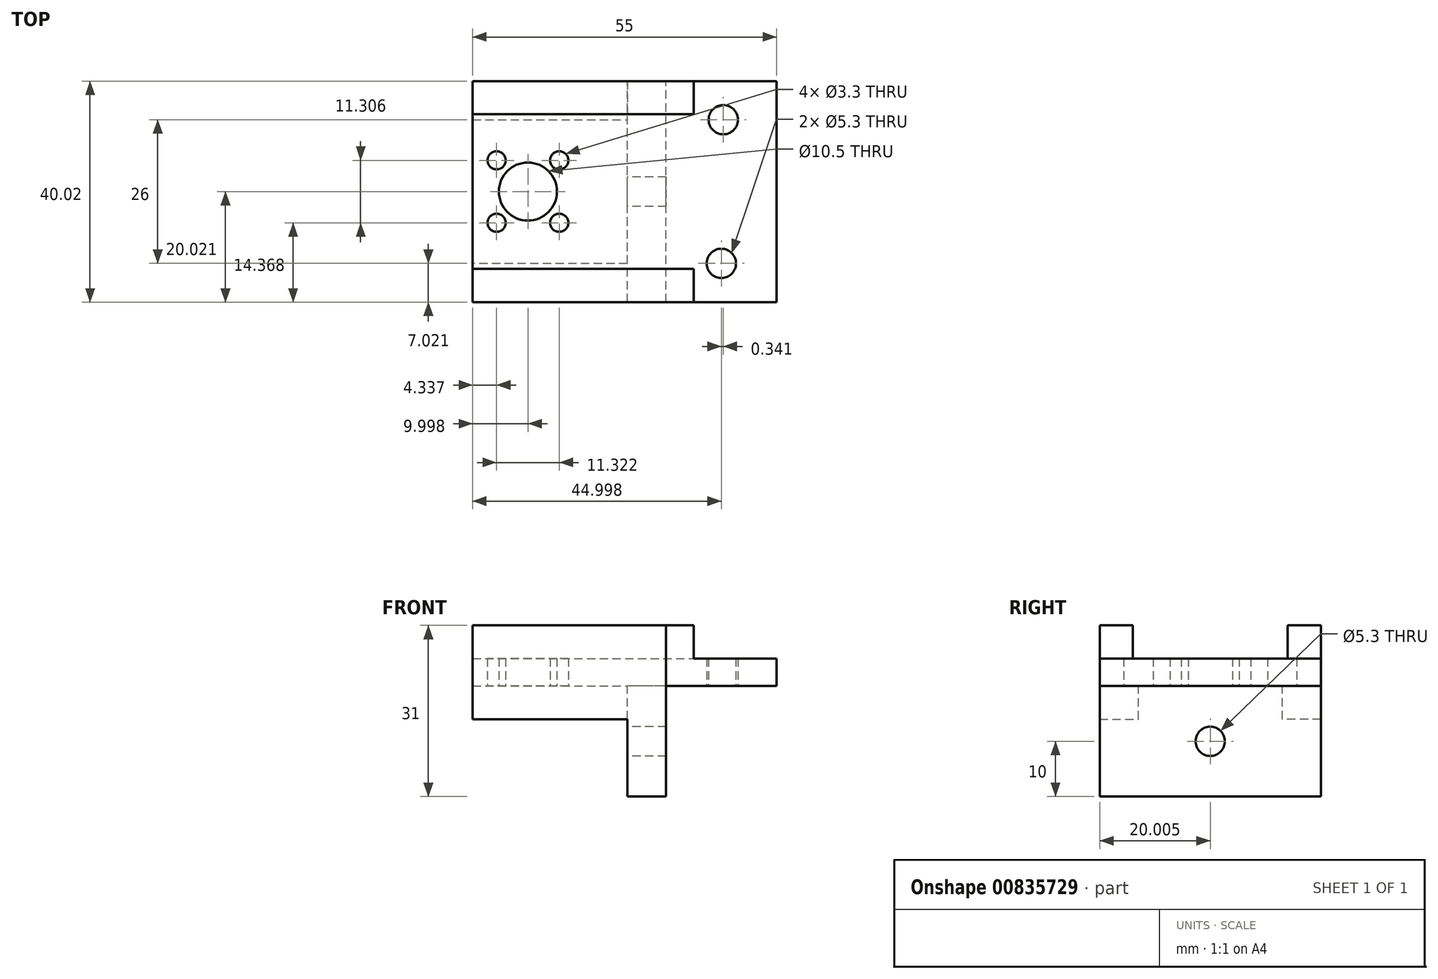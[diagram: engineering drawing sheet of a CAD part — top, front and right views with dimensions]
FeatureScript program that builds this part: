
annotation { "Feature Type Name" : "Feature", "Feature Type Description" : "" }
export const myFeature = defineFeature(function(context is Context, id is Id, definition is map)
    precondition{}
    {
        {
            var Q0;
            Q0=qCreatedBy(makeId("Top.planeOp"),FACE);
            var sketch = newSketch(context, id + "F0", { "sketchPlane" : qUnion([Q0])});
            skLineSegment(sketch, "E0.bottom", {"start": v(-49.07, -47.43) * mm, "end": v(-69.07, -47.43) * mm});
            skLineSegment(sketch, "E0.top", {"start": v(-49.07, -7.43) * mm, "end": v(-69.07, -7.43) * mm});
            skLineSegment(sketch, "E0.left", {"start": v(-49.07, -47.43) * mm, "end": v(-49.07, -7.43) * mm});
            skLineSegment(sketch, "E0.right", {"start": v(-69.07, -47.43) * mm, "end": v(-69.07, -7.43) * mm});
            skCircle(sketch, "E1", {"center": v(-59.07, -40.43) * mm, "radius": 2.65 * mm});
            skCircle(sketch, "E2", {"center": v(-58.73, -14.43) * mm, "radius": 2.65 * mm});
            skLineSegment(sketch, "E3.bottom", {"start": v(-69.07, -7.43) * mm, "end": v(-99.07, -7.43) * mm});
            skLineSegment(sketch, "E3.top", {"start": v(-69.07, -47.45) * mm, "end": v(-99.17, -47.45) * mm});
            skLineSegment(sketch, "E3.left", {"start": v(-69.07, -7.43) * mm, "end": v(-69.07, -47.45) * mm});
            skCircle(sketch, "E4", {"center": v(-94.07, -27.43) * mm, "radius": 5.25 * mm});
            skLineSegment(sketch, "E5.bottom", {"start": v(-99.07, -7.43) * mm, "end": v(-104.07, -7.43) * mm});
            skLineSegment(sketch, "E5.top", {"start": v(-99.17, -47.45) * mm, "end": v(-104.07, -47.45) * mm});
            skLineSegment(sketch, "E5.right", {"start": v(-104.07, -7.43) * mm, "end": v(-104.07, -47.45) * mm});
            skCircle(sketch, "E6", {"center": v(-99.73, -21.78) * mm, "radius": 1.65 * mm});
            skCircle(sketch, "E7", {"center": v(-88.41, -21.78) * mm, "radius": 1.65 * mm});
            skCircle(sketch, "E8", {"center": v(-88.41, -33.08) * mm, "radius": 1.65 * mm});
            skCircle(sketch, "E9", {"center": v(-99.73, -33.08) * mm, "radius": 1.65 * mm});
            skLineSegment(sketch, "E10.right", {"start": v(-104.07, -17.43) * mm, "end": v(-104.07, -37.43) * mm});
            skSolve(sketch);
        }
        {
            var Q0;
            {var subQ4=sQuery(id+"F0.wireOp",EDGE,"E3.bottom");Q0=makeQuery(id+"F0.imprint","IMPRINT",FACE,{"disambiguationData":[TD([[makeQuery(id+"F0.imprint","IMPRINT",EDGE,{"derivedFrom":subQ4}),1.0]])]});}
            var Q1;
            {var subQ1=sQuery(id+"F0.wireOp",EDGE,"E0.bottom");Q1=makeQuery(id+"F0.imprint","IMPRINT",FACE,{"disambiguationData":[TD([[makeQuery(id+"F0.imprint","IMPRINT",EDGE,{"derivedFrom":subQ1}),-1.0]])]});}
            extrude(context, id + "F1", {"entities" : qUnion([Q0, Q1]), "depth" : 5 * mm});
        }
        {
            var Q0;
            Q0=makeQuery(id+"F1.opExtrude","CAP_FACE",FACE,{"disambiguationData":[OSD([sQuery(id+"F0.wireOp",EDGE,"E0.bottom"),sQuery(id+"F0.wireOp",EDGE,"E0.top"),sQuery(id+"F0.wireOp",EDGE,"E0.left"),sQuery(id+"F0.wireOp",EDGE,"E1"),sQuery(id+"F0.wireOp",EDGE,"f49cba7f-fd84-41ad-989c-ae2e0b93f62a"),sQuery(id+"F0.wireOp",EDGE,"E2"),sQuery(id+"F0.wireOp",EDGE,"E3.bottom"),sQuery(id+"F0.wireOp",EDGE,"E3.top"),sQuery(id+"F0.wireOp",EDGE,"E3.left"),sQuery(id+"F0.wireOp",EDGE,"E4"),sQuery(id+"F0.wireOp",EDGE,"E5.bottom"),sQuery(id+"F0.wireOp",EDGE,"E5.top"),sQuery(id+"F0.wireOp",EDGE,"E5.right"),sQuery(id+"F0.wireOp",EDGE,"E6"),sQuery(id+"F0.wireOp",EDGE,"E7"),sQuery(id+"F0.wireOp",EDGE,"E8"),sQuery(id+"F0.wireOp",EDGE,"E9"),sQuery(id+"F0.wireOp",EDGE,"E10.right")])],"isStart":false});
            var sketch = newSketch(context, id + "F2", { "sketchPlane" : qUnion([Q0])});
            skLineSegment(sketch, "E11.bottom", {"start": v(-104.07, -7.43) * mm, "end": v(-64.07, -7.43) * mm});
            skLineSegment(sketch, "E11.top", {"start": v(-104.07, -13.43) * mm, "end": v(-64.07, -13.43) * mm});
            skLineSegment(sketch, "E11.left", {"start": v(-104.07, -7.43) * mm, "end": v(-104.07, -13.43) * mm});
            skLineSegment(sketch, "E11.right", {"start": v(-64.07, -7.43) * mm, "end": v(-64.07, -13.43) * mm});
            skLineSegment(sketch, "E12.bottom", {"start": v(-104.07, -47.45) * mm, "end": v(-64.07, -47.45) * mm});
            skLineSegment(sketch, "E12.top", {"start": v(-104.07, -41.45) * mm, "end": v(-64.07, -41.45) * mm});
            skLineSegment(sketch, "E12.left", {"start": v(-104.07, -47.45) * mm, "end": v(-104.07, -41.45) * mm});
            skLineSegment(sketch, "E12.right", {"start": v(-64.07, -47.45) * mm, "end": v(-64.07, -41.45) * mm});
            skLineSegment(sketch, "E13.bottom", {"start": v(-64.07, -13.43) * mm, "end": v(-64.07, -13.43) * mm});
            skLineSegment(sketch, "E13.top", {"start": v(-64.07, -41.45) * mm, "end": v(-64.07, -41.45) * mm});
            skLineSegment(sketch, "E13.left", {"start": v(-64.07, -13.43) * mm, "end": v(-64.07, -41.45) * mm});
            skLineSegment(sketch, "E13.right", {"start": v(-64.07, -13.43) * mm, "end": v(-64.07, -41.45) * mm});
            skLineSegment(sketch, "E14.bottom", {"start": v(-70.07, -13.43) * mm, "end": v(-64.07, -13.43) * mm});
            skLineSegment(sketch, "E14.top", {"start": v(-70.07, -41.45) * mm, "end": v(-64.07, -41.45) * mm});
            skLineSegment(sketch, "E14.left", {"start": v(-70.07, -13.43) * mm, "end": v(-70.07, -41.45) * mm});
            skSolve(sketch);
        }
        {
            var Q0;
            Q0=makeQuery(id+"F2.imprint","IMPRINT",FACE,{"disambiguationData":[TD([[makeQuery(id+"F2.imprint","IMPRINT",EDGE,{"derivedFrom":sQuery(id+"F2.wireOp",EDGE,"E11.bottom")}),1.0]])]});
            var Q1;
            Q1=makeQuery(id+"F2.imprint","IMPRINT",FACE,{"disambiguationData":[TD([[makeQuery(id+"F2.imprint","IMPRINT",EDGE,{"derivedFrom":sQuery(id+"F2.wireOp",EDGE,"E14.bottom")}),-1.0]])]});
            var Q2;
            Q2=makeQuery(id+"F2.imprint","IMPRINT",FACE,{"disambiguationData":[TD([[makeQuery(id+"F2.imprint","IMPRINT",EDGE,{"derivedFrom":sQuery(id+"F2.wireOp",EDGE,"E12.top")}),-1.0]])]});
            extrude(context, id + "F3", {"entities" : qUnion([Q0, Q1, Q2]), "operationType" : NewBodyOperationType.ADD, "depth" : 6 * mm});
        }
        {
            var Q0;
            {var subQ4=sQuery(id+"F0.wireOp",EDGE,"E3.bottom");Q0=makeQuery(id+"F0.imprint","IMPRINT",FACE,{"disambiguationData":[TD([[makeQuery(id+"F0.imprint","IMPRINT",EDGE,{"derivedFrom":subQ4}),1.0]])]});}
            var sketch = newSketch(context, id + "F4", { "sketchPlane" : qUnion([Q0])});
            skLineSegment(sketch, "E15.bottom", {"start": v(-69.07, -47.45) * mm, "end": v(-76.07, -47.45) * mm});
            skLineSegment(sketch, "E15.top", {"start": v(-69.07, -7.45) * mm, "end": v(-76.07, -7.45) * mm});
            skLineSegment(sketch, "E15.left", {"start": v(-69.07, -47.45) * mm, "end": v(-69.07, -7.45) * mm});
            skLineSegment(sketch, "E15.right", {"start": v(-76.07, -47.45) * mm, "end": v(-76.07, -7.45) * mm});
            skSolve(sketch);
        }
        {
            var Q0;
            {var subQ2=sQuery(id+"F4.wireOp",EDGE,"E15.bottom");Q0=makeQuery(id+"F4.imprint","IMPRINT",FACE,{"disambiguationData":[TD([[makeQuery(id+"F4.imprint","IMPRINT",EDGE,{"derivedFrom":subQ2}),-1.0]])]});}
            extrude(context, id + "F5", {"entities" : qUnion([Q0]), "operationType" : NewBodyOperationType.ADD, "oppositeDirection" : true, "depth" : 20 * mm});
        }
        {
            var Q0;
            Q0=makeQuery(id+"F5.opExtrude","SWEPT_FACE",FACE,{"disambiguationData":[OSD([sQuery(id+"F4.wireOp",EDGE,"E15.right")])]});
            var sketch = newSketch(context, id + "F6", { "sketchPlane" : qUnion([Q0])});
            skCircle(sketch, "E16", {"center": v(27.45, -10) * mm, "radius": 2.65 * mm});
            skSolve(sketch);
        }
        {
            var Q0;
            Q0=makeQuery(id+"F6.imprint","IMPRINT",FACE,{"disambiguationData":[TD([[makeQuery(id+"F6.imprint","IMPRINT",EDGE,{"derivedFrom":sQuery(id+"F6.wireOp",EDGE,"E16")}),1.0]])]});
            extrude(context, id + "F7", {"entities" : qUnion([Q0]), "operationType" : NewBodyOperationType.REMOVE, "oppositeDirection" : true, "depth" : 25 * mm});
        }
        {
            var Q0;
            {var subQ4=sQuery(id+"F0.wireOp",EDGE,"E3.bottom");Q0=makeQuery(id+"F0.imprint","IMPRINT",FACE,{"disambiguationData":[TD([[makeQuery(id+"F0.imprint","IMPRINT",EDGE,{"derivedFrom":subQ4}),1.0]])]});}
            var sketch = newSketch(context, id + "F8", { "sketchPlane" : qUnion([Q0])});
            skLineSegment(sketch, "E17.bottom", {"start": v(-76.07, -47.45) * mm, "end": v(-104.07, -47.45) * mm});
            skLineSegment(sketch, "E17.top", {"start": v(-76.07, -40.45) * mm, "end": v(-104.07, -40.45) * mm});
            skLineSegment(sketch, "E17.left", {"start": v(-76.07, -47.45) * mm, "end": v(-76.07, -40.45) * mm});
            skLineSegment(sketch, "E17.right", {"start": v(-104.07, -47.45) * mm, "end": v(-104.07, -40.45) * mm});
            skLineSegment(sketch, "E18.bottom", {"start": v(-104.07, -7.43) * mm, "end": v(-76.07, -7.43) * mm});
            skLineSegment(sketch, "E18.top", {"start": v(-104.07, -14.43) * mm, "end": v(-76.07, -14.43) * mm});
            skLineSegment(sketch, "E18.left", {"start": v(-104.07, -7.43) * mm, "end": v(-104.07, -14.43) * mm});
            skLineSegment(sketch, "E18.right", {"start": v(-76.07, -7.43) * mm, "end": v(-76.07, -14.43) * mm});
            skSolve(sketch);
        }
        {
            var Q0;
            Q0=makeQuery(id+"F8.imprint","IMPRINT",FACE,{"disambiguationData":[TD([[makeQuery(id+"F8.imprint","IMPRINT",EDGE,{"derivedFrom":sQuery(id+"F8.wireOp",EDGE,"E17.top")}),1.0]])]});
            var Q1;
            Q1=makeQuery(id+"F8.imprint","IMPRINT",FACE,{"disambiguationData":[TD([[makeQuery(id+"F8.imprint","IMPRINT",EDGE,{"derivedFrom":sQuery(id+"F8.wireOp",EDGE,"E18.top")}),1.0]])]});
            extrude(context, id + "F9", {"entities" : qUnion([Q0, Q1]), "operationType" : NewBodyOperationType.ADD, "oppositeDirection" : true, "depth" : 6 * mm});
        }
    });
